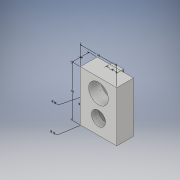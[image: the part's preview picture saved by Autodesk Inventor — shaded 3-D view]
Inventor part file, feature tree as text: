
AUTODESK INVENTOR PART (.ipt)
format: ipt  version: 2018 (Build 220112000, 112)  size: 159,744 bytes
history: native  units: in
note: dims shown in document units (in); Inventor stores cm internally (conversion verified against a paired STEP export)
features: other x11, sketch x3, hole x2, extrude x1
ambient origin geometry x8: Origin, YZ Plane, XZ Plane, XY Plane, X Axis, Y Axis, Z Axis, Center Point
bodies: Solid1 (feature_tree)
feature tree (17):
  other  "Annotations"
  extrude  "Extrusion1"  Depth=0.3in
  hole  "Hole5"  [1 undecoded]
  hole  "Hole6"  [1 undecoded]
  sketch  "Sketch1"  dims[d0=0.65in d1=0.3in]
  sketch  "Sketch8"  dims[d2=0.2in d3=0.05in]
  sketch  "Sketch9"  dims[d4=0.9in d5=0.0in d38=0.265in d39=0.11in d40=0.75in d41=0.25in d42=0.13in d43=0.5635in d44=1.0in d45=0.8108in d46=0.255in d47=0.2in d48=0.75in d49=0.35in d50=0.22in d51=0.5635in d52=1.0in d53=0.8108in d54=0.0in d55=0.3937in d56=0.65in d57=0.0in d58=0.3937in d59=0.9in d60=2.2191in d61=0.3243in d62=-0.1451in d63=0.35in d64=2.1882in d65=0.1683in d66=-0.1585in d67=0.25in d68=0.1043in d69=0.3248in d70=0.3in d71=0.0in d72=0.3937in d73=0.05in d74=2.4418in d75=0.2812in d76=0.0588in d77=0.2in d78=1.2214in d79=0.11in d80=0.1854in d81=0.1939in d82=0.2in d83=0.3837in d31=1.0in d32=1.0in]
  other  "Linear Dimension 1"
  other  "Linear Dimension 2"
  other  "Diameter Dimension 1"
  other  "Diameter Dimension 2"
  other  "Linear Dimension 3"
  other  "Linear Dimension 4"
  other  "Diameter Dimension 3"
  other  "Diameter Dimension 4"
  other  "Linear Dimension 5"
  other  "Linear Dimension 6"
note: 2 required parameter values undecoded (feature->parameter linkage not recoverable at this tier; creation-order binding heuristic only, values carry confidence <= 0.55)
